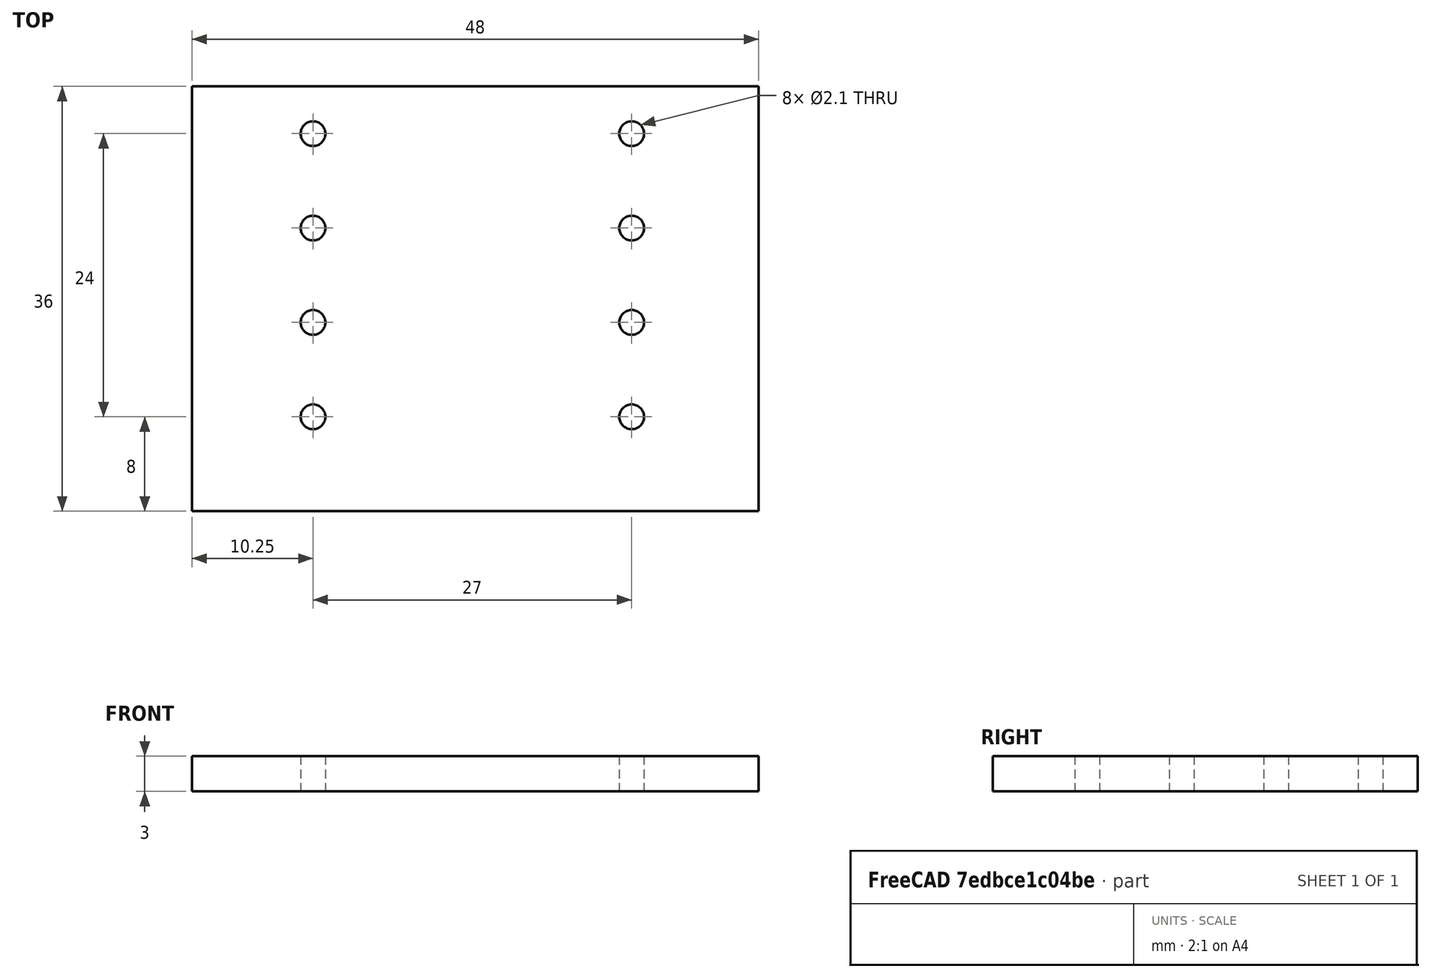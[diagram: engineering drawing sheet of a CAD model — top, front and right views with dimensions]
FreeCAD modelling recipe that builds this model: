
FCSTD DOCUMENT  (FreeCAD 0.15R4671 (Git))
Label: just_a_plate
License: All rights reserved
LicenseURL: http://en.wikipedia.org/wiki/All_rights_reserved
objects: Part::Cylinder×8, Part::MultiFuse×3, Part::Box×1, Part::Cut×1
note: 13 computed .brp shape members not serialized (recipe doc carries the construction recipe); baked Part::Feature solids carry a one-line shape summary decoded from their .brp

FEATURE [Part::Box] Box  label="Cube"
  Height = 3
  Length = 48
  Width = 36
FEATURE [Part::Cylinder] Cylinder019
  Angle = 360
  Height = 10
  Placement = pos=(-4,16,10.25) rot=(0,1,0;1.5708rad)
  Radius = 1.05
FEATURE [Part::Cylinder] Cylinder020
  Angle = 360
  Height = 10
  Placement = pos=(-4,24,10.25) rot=(0,1,0;1.5708rad)
  Radius = 1.05
FEATURE [Part::Cylinder] Cylinder021
  Angle = 360
  Height = 10
  Placement = pos=(-4,32,10.25) rot=(0,1,0;1.5708rad)
  Radius = 1.05
FEATURE [Part::Cylinder] Cylinder022
  Angle = 360
  Height = 10
  Placement = pos=(-4,8,10.25) rot=(0,1,0;1.5708rad)
  Radius = 1.05
FEATURE [Part::MultiFuse] Fusion003
  Placement = pos=(0,0,0) rot=(0,1,0;1.5708rad)
  Shapes = -> [Cylinder019,Cylinder021,Cylinder020,Cylinder022]
FEATURE [Part::Cylinder] Cylinder023
  Angle = 360
  Height = 10
  Placement = pos=(-4,16,10.25) rot=(0,1,0;1.5708rad)
  Radius = 1.05
FEATURE [Part::Cylinder] Cylinder024
  Angle = 360
  Height = 10
  Placement = pos=(-4,24,10.25) rot=(0,1,0;1.5708rad)
  Radius = 1.05
FEATURE [Part::Cylinder] Cylinder025
  Angle = 360
  Height = 10
  Placement = pos=(-4,32,10.25) rot=(0,1,0;1.5708rad)
  Radius = 1.05
FEATURE [Part::Cylinder] Cylinder026
  Angle = 360
  Height = 10
  Placement = pos=(-4,8,10.25) rot=(0,1,0;1.5708rad)
  Radius = 1.05
FEATURE [Part::MultiFuse] Fusion004
  Placement = pos=(27,0,0) rot=(0,1,0;1.5708rad)
  Shapes = -> [Cylinder023,Cylinder025,Cylinder024,Cylinder026]
FEATURE [Part::MultiFuse] Fusion
  Shapes = -> [Fusion003,Fusion004]
FEATURE [Part::Cut] Cut
  Base = -> Box
  Tool = -> Fusion
